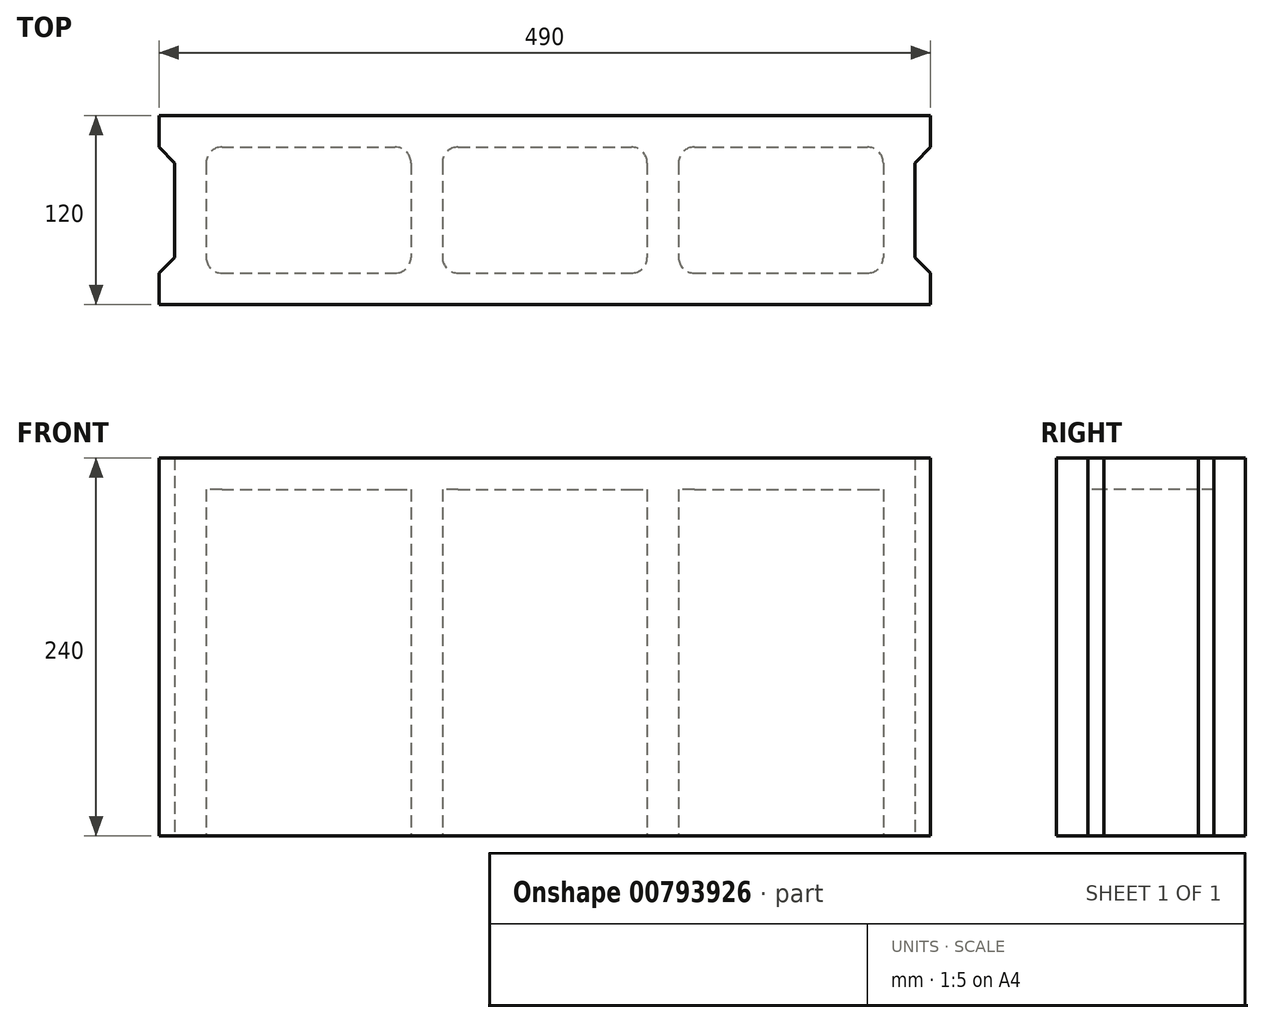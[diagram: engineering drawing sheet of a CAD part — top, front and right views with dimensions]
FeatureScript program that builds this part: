
annotation { "Feature Type Name" : "Feature", "Feature Type Description" : "" }
export const myFeature = defineFeature(function(context is Context, id is Id, definition is map)
    precondition{}
    {
        {
            var Q0;
            Q0=qCreatedBy(makeId("Top.planeOp"),FACE);
            var sketch = newSketch(context, id + "F0", { "sketchPlane" : qUnion([Q0])});
            skLineSegment(sketch, "E0.bottom", {"start": v(0, 0) * mm, "end": v(490, 0) * mm});
            skLineSegment(sketch, "E0.top", {"start": v(0, 120) * mm, "end": v(490, 120) * mm});
            skLineSegment(sketch, "E0.left", {"start": v(0, 0) * mm, "end": v(0, 120) * mm});
            skLineSegment(sketch, "E0.right", {"start": v(490, 0) * mm, "end": v(490, 120) * mm});
            skPoint(sketch, "E1.oppositeSnap0", {"position": v(0, 60) * mm});
            skLineSegment(sketch, "E1.bottom", {"start": v(40, 100) * mm, "end": v(150, 100) * mm});
            skLineSegment(sketch, "E1.top", {"start": v(40, 20) * mm, "end": v(150, 20) * mm});
            skLineSegment(sketch, "E1.left", {"start": v(30, 90) * mm, "end": v(30, 30) * mm});
            skLineSegment(sketch, "E1.right", {"start": v(160, 90) * mm, "end": v(160, 30) * mm});
            skPoint(sketch, "E2.visualSharp", {"position": v(160, 100) * mm});
            skArc(sketch, "E2.filletArc", {"start": v(160, 90) * mm, "mid": v(157.07, 97.07) * mm, "end": v(150, 100) * mm});
            skPoint(sketch, "E3.visualSharp", {"position": v(160, 20) * mm});
            skArc(sketch, "E3.filletArc", {"start": v(150, 20) * mm, "mid": v(157.07, 22.93) * mm, "end": v(160, 30) * mm});
            skArc(sketch, "E4.filletArc", {"start": v(30, 30) * mm, "mid": v(32.93, 22.93) * mm, "end": v(40, 20) * mm});
            skArc(sketch, "E5.filletArc", {"start": v(40, 100) * mm, "mid": v(32.93, 97.07) * mm, "end": v(30, 90) * mm});
            skLineSegment(sketch, "E6.1.0.0", {"start": v(190, 100) * mm, "end": v(300, 100) * mm});
            skArc(sketch, "E6.1.0.1", {"start": v(190, 100) * mm, "mid": v(182.93, 97.07) * mm, "end": v(180, 90) * mm});
            skLineSegment(sketch, "E6.1.0.2", {"start": v(180, 90) * mm, "end": v(180, 30) * mm});
            skArc(sketch, "E6.1.0.3", {"start": v(180, 30) * mm, "mid": v(182.93, 22.93) * mm, "end": v(190, 20) * mm});
            skLineSegment(sketch, "E6.1.0.4", {"start": v(190, 20) * mm, "end": v(300, 20) * mm});
            skArc(sketch, "E6.1.0.5", {"start": v(300, 20) * mm, "mid": v(307.07, 22.93) * mm, "end": v(310, 30) * mm});
            skLineSegment(sketch, "E6.1.0.6", {"start": v(310, 90) * mm, "end": v(310, 30) * mm});
            skArc(sketch, "E6.1.0.7", {"start": v(310, 90) * mm, "mid": v(307.07, 97.07) * mm, "end": v(300, 100) * mm});
            skLineSegment(sketch, "E6.2.0.0", {"start": v(340, 100) * mm, "end": v(450, 100) * mm});
            skArc(sketch, "E6.2.0.1", {"start": v(340, 100) * mm, "mid": v(332.93, 97.07) * mm, "end": v(330, 90) * mm});
            skLineSegment(sketch, "E6.2.0.2", {"start": v(330, 90) * mm, "end": v(330, 30) * mm});
            skArc(sketch, "E6.2.0.3", {"start": v(330, 30) * mm, "mid": v(332.93, 22.93) * mm, "end": v(340, 20) * mm});
            skLineSegment(sketch, "E6.2.0.4", {"start": v(340, 20) * mm, "end": v(450, 20) * mm});
            skArc(sketch, "E6.2.0.5", {"start": v(450, 20) * mm, "mid": v(457.07, 22.93) * mm, "end": v(460, 30) * mm});
            skLineSegment(sketch, "E6.2.0.6", {"start": v(460, 90) * mm, "end": v(460, 30) * mm});
            skArc(sketch, "E6.2.0.7", {"start": v(460, 90) * mm, "mid": v(457.07, 97.07) * mm, "end": v(450, 100) * mm});
            skLineSegment(sketch, "E6.direction1", {"start": v(30, 30) * mm, "end": v(180, 30) * mm, "construction": true});
            skLineSegment(sketch, "E7", {"start": v(0, 120) * mm, "end": v(0, 100) * mm});
            skLineSegment(sketch, "E8", {"start": v(10, 90) * mm, "end": v(0, 100) * mm});
            skLineSegment(sketch, "E9", {"start": v(10, 90) * mm, "end": v(10, 60) * mm});
            skLineSegment(sketch, "E10", {"start": v(0, 60) * mm, "end": v(490, 60) * mm, "construction": true});
            skLineSegment(sketch, "E11.MirrorCS", {"start": v(0, 0) * mm, "end": v(0, 20) * mm});
            skLineSegment(sketch, "E12.MirrorCS", {"start": v(10, 30) * mm, "end": v(10, 60) * mm});
            skLineSegment(sketch, "E13.MirrorCS", {"start": v(10, 30) * mm, "end": v(0, 20) * mm});
            skLineSegment(sketch, "E14", {"start": v(245, 120) * mm, "end": v(245, 0) * mm, "construction": true});
            skLineSegment(sketch, "E15.MirrorCS", {"start": v(480, 30) * mm, "end": v(490, 20) * mm});
            skLineSegment(sketch, "E16.MirrorCS", {"start": v(490, 0) * mm, "end": v(490, 20) * mm});
            skLineSegment(sketch, "E17.MirrorCS", {"start": v(480, 30) * mm, "end": v(480, 60) * mm});
            skLineSegment(sketch, "E18.MirrorCS", {"start": v(480, 90) * mm, "end": v(480, 60) * mm});
            skLineSegment(sketch, "E19.MirrorCS", {"start": v(490, 120) * mm, "end": v(490, 100) * mm});
            skLineSegment(sketch, "E20.MirrorCS", {"start": v(480, 90) * mm, "end": v(490, 100) * mm});
            skLineSegment(sketch, "E21", {"start": v(95, 20) * mm, "end": v(95, 100) * mm, "construction": true});
            skLineSegment(sketch, "E22", {"start": v(395, 20) * mm, "end": v(395, 100) * mm, "construction": true});
            skSolve(sketch);
        }
        {
            var Q0;
            {var subQ3=sQuery(id+"F0.wireOp",EDGE,"E0.bottom");Q0=makeQuery(id+"F0.imprint","IMPRINT",FACE,{"disambiguationData":[TD([[makeQuery(id+"F0.imprint","IMPRINT",EDGE,{"derivedFrom":subQ3}),1.0]])]});}
            var Q1;
            Q1=makeQuery(id+"F0.imprint","IMPRINT",FACE,{"disambiguationData":[TD([[makeQuery(id+"F0.imprint","IMPRINT",EDGE,{"derivedFrom":sQuery(id+"F0.wireOp",EDGE,"E1.bottom")}),-1.0]])]});
            var Q2;
            Q2=makeQuery(id+"F0.imprint","IMPRINT",FACE,{"disambiguationData":[TD([[makeQuery(id+"F0.imprint","IMPRINT",EDGE,{"derivedFrom":sQuery(id+"F0.wireOp",EDGE,"E6.1.0.0")}),-1.0]])]});
            var Q3;
            Q3=makeQuery(id+"F0.imprint","IMPRINT",FACE,{"disambiguationData":[TD([[makeQuery(id+"F0.imprint","IMPRINT",EDGE,{"derivedFrom":sQuery(id+"F0.wireOp",EDGE,"E6.2.0.0")}),-1.0]])]});
            extrude(context, id + "F1", {"entities" : qUnion([Q0, Q1, Q2, Q3]), "depth" : 240 * mm, "offsetDistance" : 25 * mm});
        }
        {
            var Q0;
            Q0=makeQuery(id+"F0.imprint","IMPRINT",FACE,{"disambiguationData":[TD([[makeQuery(id+"F0.imprint","IMPRINT",EDGE,{"derivedFrom":sQuery(id+"F0.wireOp",EDGE,"E1.bottom")}),-1.0]])]});
            var Q1;
            Q1=makeQuery(id+"F0.imprint","IMPRINT",FACE,{"disambiguationData":[TD([[makeQuery(id+"F0.imprint","IMPRINT",EDGE,{"derivedFrom":sQuery(id+"F0.wireOp",EDGE,"E6.1.0.0")}),-1.0]])]});
            var Q2;
            Q2=makeQuery(id+"F0.imprint","IMPRINT",FACE,{"disambiguationData":[TD([[makeQuery(id+"F0.imprint","IMPRINT",EDGE,{"derivedFrom":sQuery(id+"F0.wireOp",EDGE,"E6.2.0.0")}),-1.0]])]});
            extrude(context, id + "F2", {"entities" : qUnion([Q0, Q1, Q2]), "operationType" : NewBodyOperationType.REMOVE, "depth" : 220 * mm, "offsetDistance" : 25 * mm});
        }
        {
            var Q0;
            Q0=qCreatedBy(makeId("Right.planeOp"),FACE);
            var Q1;
            Q1=sQuery(id+"F0.wireOp",EDGE,"E21");
            cPlane(context, id + "F3", {"entities" : qUnion([Q0, Q1]), "cplaneType" : CPlaneType.LINE_ANGLE, "offset" : 100 * mm, "angle" : 0 * degree, "width" : 150 * mm, "height" : 150 * mm});
        }
    });
